# Revit family: 67305007_Fogão 6 bocas
name_source: partatom
category: Mechanical Equipment
units: mm (PartAtom-declared; Revit-internal decimal feet)

## family parameters
Always vertical = Yes
Classification = None
Cut with Voids When Loaded = No
Part Type = Normal
Room Calculation Point = No
Round Connector Dimension = Use Diameter
Shared = No
Work Plane-Based = No

## types (1)
- 67305007_Fogão 6 bocas
    Bico Injetor GLP = 1.2
    Bico Injetor GN = 1.8
    Consumos total de gás GLP = 2,4 Kg/h
    Consumos total de gás GN = 3,3 m³/h
    Description = Fogão a gás 06 bocas - Countertop
    Draw by = Projetos e Eventos Consultoria
    Manufacturer = Tramontina
    Model = 67305007
    Peso = 0,00 Kg
    Potência queimadores = 6 x 6 kW = 36 kW
    Pressão de trabalho GLP = 0.0 bar
    Pressão de trabalho GN = 0.0 bar
    RFA Designer = Projetos e Eventos Consultoria
    Regulagem do ar GLP = 8 mm
    Regulagem do ar GN = 3 mm

## geometry (parser evidence)
native form markers: Sweep x17
no freeform markers — native parametric forms only
